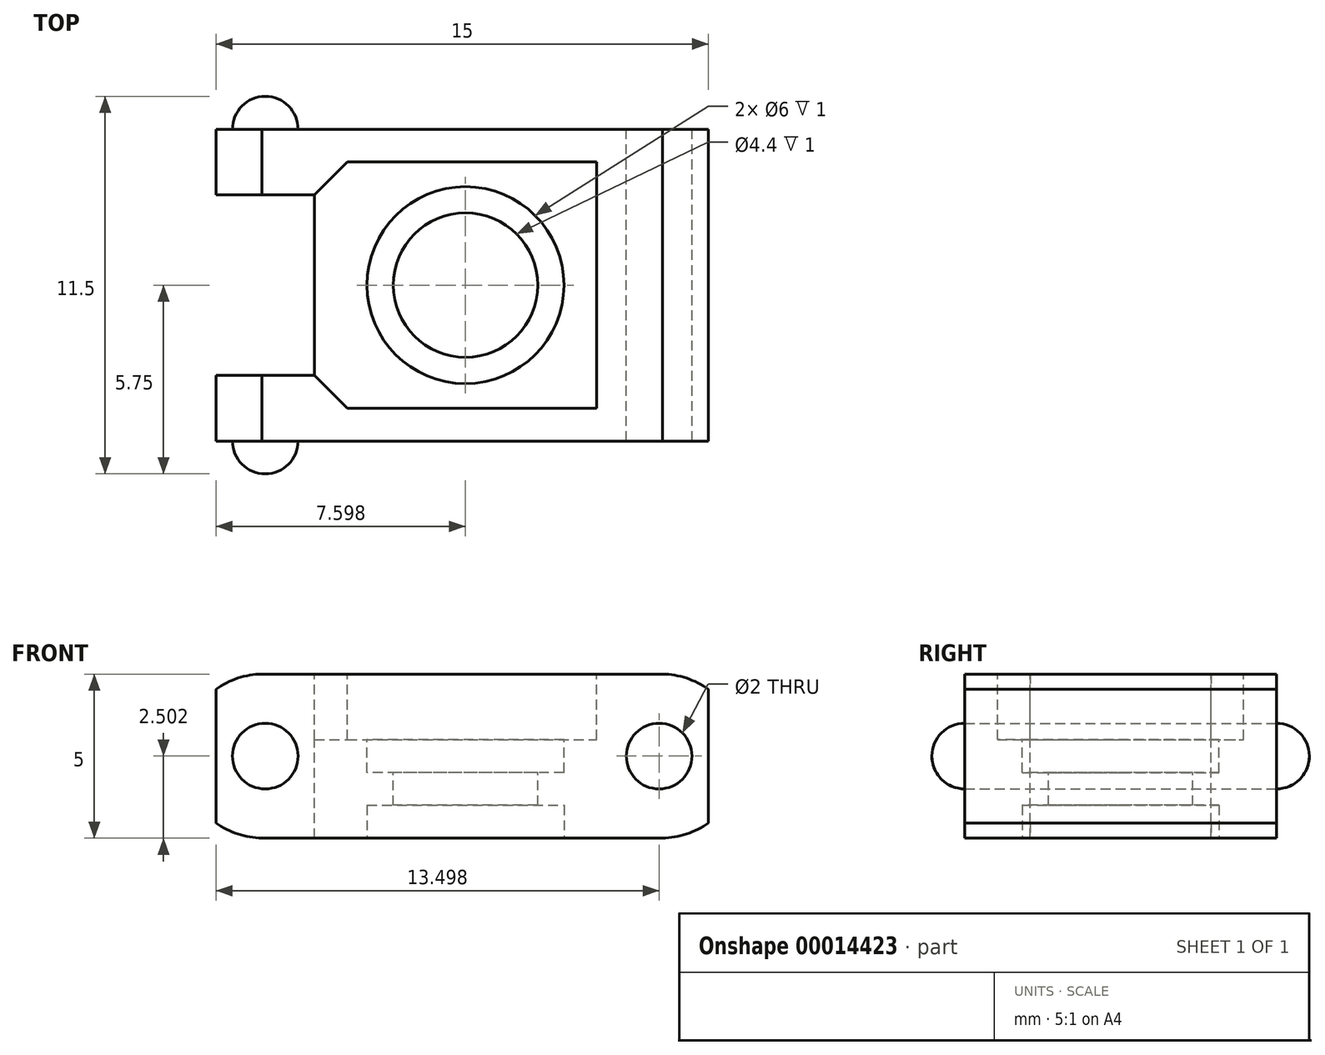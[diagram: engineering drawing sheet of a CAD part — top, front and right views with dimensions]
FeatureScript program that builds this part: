
annotation { "Feature Type Name" : "Feature", "Feature Type Description" : "" }
export const myFeature = defineFeature(function(context is Context, id is Id, definition is map)
    precondition{}
    {
        {
            var Q0;
            Q0=qCreatedBy(makeId("Front.planeOp"),FACE);
            var sketch = newSketch(context, id + "F0", { "sketchPlane" : qUnion([Q0])});
            skLineSegment(sketch, "E0.bottom", {"start": v(28.09, 13.2) * mm, "end": v(43.09, 13.2) * mm});
            skLineSegment(sketch, "E0.top", {"start": v(28.09, 8.2) * mm, "end": v(43.09, 8.2) * mm});
            skLineSegment(sketch, "E0.left", {"start": v(28.09, 13.2) * mm, "end": v(28.09, 8.2) * mm});
            skLineSegment(sketch, "E0.right", {"start": v(43.09, 13.2) * mm, "end": v(43.09, 8.2) * mm});
            skLineSegment(sketch, "E1", {"start": v(35.59, 8.2) * mm, "end": v(35.59, 13.2) * mm, "construction": true});
            skPoint(sketch, "E2", {"position": v(31.09, 13.2) * mm});
            skLineSegment(sketch, "E3", {"start": v(28.09, 8.2) * mm, "end": v(31.09, 13.2) * mm, "construction": true});
            skLineSegment(sketch, "E4", {"start": v(31.09, 13.2) * mm, "end": v(31.09, 8.2) * mm, "construction": true});
            skLineSegment(sketch, "E5", {"start": v(31.09, 8.2) * mm, "end": v(28.09, 13.2) * mm, "construction": true});
            skCircle(sketch, "E6", {"center": v(29.59, 10.7) * mm, "radius": 1 * mm});
            skLineSegment(sketch, "E7", {"start": v(29.59, 13.2) * mm, "end": v(29.59, 8.2) * mm, "construction": true});
            skLineSegment(sketch, "E8", {"start": v(28.09, 10.7) * mm, "end": v(31.09, 10.7) * mm, "construction": true});
            skArc(sketch, "E9", {"start": v(29.59, 13.2) * mm, "mid": v(27.04, 10.7) * mm, "end": v(29.59, 8.2) * mm});
            skCircle(sketch, "E10.0.MirrorC", {"center": v(41.59, 10.7) * mm, "radius": 1 * mm});
            skArc(sketch, "E11.0.MirrorCS", {"start": v(41.59, 13.2) * mm, "mid": v(44.14, 10.7) * mm, "end": v(41.59, 8.2) * mm});
            skSolve(sketch);
        }
        {
            var Q0;
            {var subQ5=sQuery(id+"F0.wireOp",EDGE,"E0.right");Q0=makeQuery(id+"F0.imprint","IMPRINT",FACE,{"disambiguationData":[TD([[makeQuery(id+"F0.imprint","IMPRINT",EDGE,{"derivedFrom":subQ5}),-1.0]])]});}
            var Q1;
            Q1=makeQuery(id+"F0.imprint","IMPRINT",FACE,{"disambiguationData":[TD([[makeQuery(id+"F0.imprint","IMPRINT",EDGE,{"derivedFrom":sQuery(id+"F0.wireOp",EDGE,"E6")}),-1.0]])]});
            var Q2;
            {var subQ5=sQuery(id+"F0.wireOp",EDGE,"E0.left");Q2=makeQuery(id+"F0.imprint","IMPRINT",FACE,{"disambiguationData":[TD([[makeQuery(id+"F0.imprint","IMPRINT",EDGE,{"derivedFrom":subQ5}),1.0]])]});}
            var Q3;
            Q3=makeQuery(id+"F0.imprint","IMPRINT",FACE,{"disambiguationData":[TD([[makeQuery(id+"F0.imprint","IMPRINT",EDGE,{"derivedFrom":sQuery(id+"F0.wireOp",EDGE,"E6")}),1.0]])]});
            var Q4;
            Q4=makeQuery(id+"F0.imprint","IMPRINT",FACE,{"disambiguationData":[TD([[makeQuery(id+"F0.imprint","IMPRINT",EDGE,{"derivedFrom":sQuery(id+"F0.wireOp",EDGE,"E10.0.MirrorC")}),-1.0]])]});
            extrude(context, id + "F1", {"entities" : qUnion([Q0, Q1, Q2, Q3, Q4]), "depth" : 9.5 * mm});
        }
        {
            var Q0;
            Q0=makeQuery(id+"F1.opExtrude","SWEPT_FACE",FACE,{"disambiguationData":[OSD([sQuery(id+"F0.wireOp",EDGE,"E0.bottom")])]});
            var sketch = newSketch(context, id + "F2", { "sketchPlane" : qUnion([Q0])});
            skLineSegment(sketch, "E12", {"start": v(35.59, 0) * mm, "end": v(35.59, -9.5) * mm, "construction": true});
            skLineSegment(sketch, "E13", {"start": v(28.09, -4.75) * mm, "end": v(43.09, -4.75) * mm, "construction": true});
            skPoint(sketch, "E14", {"position": v(31.09, 0) * mm});
            skLineSegment(sketch, "E15", {"start": v(31.09, 0) * mm, "end": v(31.09, -9.5) * mm, "construction": true});
            skPoint(sketch, "E16", {"position": v(28.09, -2) * mm});
            skLineSegment(sketch, "E17", {"start": v(28.09, -2) * mm, "end": v(31.09, -2) * mm});
            skLineSegment(sketch, "E18.0.MirrorCS", {"start": v(28.09, -7.5) * mm, "end": v(31.09, -7.5) * mm});
            skLineSegment(sketch, "E19", {"start": v(31.09, -7.5) * mm, "end": v(31.09, -2) * mm});
            skLineSegment(sketch, "E20", {"start": v(28.09, -2) * mm, "end": v(28.09, -7.5) * mm});
            skSolve(sketch);
        }
        {
            var Q0;
            Q0=makeQuery(id+"F2.imprint","IMPRINT",FACE,{"disambiguationData":[TD([[makeQuery(id+"F2.imprint","IMPRINT",EDGE,{"derivedFrom":sQuery(id+"F2.wireOp",EDGE,"E17")}),-1.0]])]});
            var Q1;
            Q1=makeQuery(id+"F2.imprint","IMPRINT",FACE,{"disambiguationData":[TD([[makeQuery(id+"F2.imprint","IMPRINT",EDGE,{"derivedFrom":sQuery(id+"F2.wireOp",EDGE,"8c34fa15-d911-4d8d-b620-4605c3a337e2.0.MirrorCS")}),-1.0]])]});
            extrude(context, id + "F3", {"entities" : qUnion([Q0, Q1]), "operationType" : NewBodyOperationType.REMOVE, "endBound" : BoundingType.THROUGH_ALL, "oppositeDirection" : true, "depth" : 25 * mm});
        }
        {
            var Q0;
            {var subQ5=sQuery(id+"F0.wireOp",EDGE,"E0.right");Q0=makeQuery(id+"F0.imprint","IMPRINT",FACE,{"disambiguationData":[TD([[makeQuery(id+"F0.imprint","IMPRINT",EDGE,{"derivedFrom":subQ5}),-1.0]])]});}
            var Q1;
            {var subQ5=sQuery(id+"F0.wireOp",EDGE,"E0.left");Q1=makeQuery(id+"F0.imprint","IMPRINT",FACE,{"disambiguationData":[TD([[makeQuery(id+"F0.imprint","IMPRINT",EDGE,{"derivedFrom":subQ5}),1.0]])]});}
            extrude(context, id + "F4", {"entities" : qUnion([Q0, Q1]), "operationType" : NewBodyOperationType.REMOVE, "endBound" : BoundingType.THROUGH_ALL, "depth" : 25 * mm});
        }
        {
            var Q0;
            Q0=makeQuery(id+"F0.imprint","IMPRINT",FACE,{"disambiguationData":[TD([[makeQuery(id+"F0.imprint","IMPRINT",EDGE,{"derivedFrom":sQuery(id+"F0.wireOp",EDGE,"E6")}),1.0]])]});
            extrude(context, id + "F5", {"entities" : qUnion([Q0]), "operationType" : NewBodyOperationType.ADD, "oppositeDirection" : true, "depth" : 1 * mm});
        }
        {
            var Q0;
            Q0=makeQuery(id+"F1.opExtrude","CAP_FACE",FACE,{"disambiguationData":[OSD([sQuery(id+"F0.wireOp",EDGE,"E0.bottom"),sQuery(id+"F0.wireOp",EDGE,"E0.top"),sQuery(id+"F0.wireOp",EDGE,"E0.left"),sQuery(id+"F0.wireOp",EDGE,"E0.right")])],"isStart":false});
            var sketch = newSketch(context, id + "F6", { "sketchPlane" : qUnion([Q0])});
            skLineSegment(sketch, "E21", {"start": v(35.59, 8.2) * mm, "end": v(35.59, 13.2) * mm, "construction": true});
            skPoint(sketch, "E22", {"position": v(31.09, 8.2) * mm});
            skPoint(sketch, "E23", {"position": v(28.09, 8.2) * mm});
            skLineSegment(sketch, "E24", {"start": v(31.09, 8.2) * mm, "end": v(31.09, 13.2) * mm, "construction": true});
            skLineSegment(sketch, "E25", {"start": v(31.09, 13.2) * mm, "end": v(28.09, 8.2) * mm, "construction": true});
            skPoint(sketch, "E26", {"position": v(28.09, 13.2) * mm});
            skLineSegment(sketch, "E27", {"start": v(28.09, 13.2) * mm, "end": v(28.09, 8.2) * mm, "construction": true});
            skLineSegment(sketch, "E28", {"start": v(31.09, 13.2) * mm, "end": v(28.09, 13.2) * mm, "construction": true});
            skLineSegment(sketch, "E29", {"start": v(28.09, 13.2) * mm, "end": v(31.09, 8.2) * mm, "construction": true});
            skCircle(sketch, "E30", {"center": v(29.59, 10.7) * mm, "radius": 1 * mm});
            skCircle(sketch, "E31.MirrorC", {"center": v(41.59, 10.7) * mm, "radius": 1 * mm});
            skSolve(sketch);
        }
        {
            var Q0;
            Q0=makeQuery(id+"F6.imprint","IMPRINT",FACE,{"disambiguationData":[TD([[makeQuery(id+"F6.imprint","IMPRINT",EDGE,{"derivedFrom":sQuery(id+"F6.wireOp",EDGE,"E30")}),1.0]])]});
            extrude(context, id + "F7", {"entities" : qUnion([Q0]), "operationType" : NewBodyOperationType.ADD, "depth" : 1 * mm, "hasSecondDirectionDraft" : true, "secondDirectionDraftAngle" : 10 * degree});
        }
        {
            var Q0;
            Q0=makeQuery(id+"F1.opExtrude","SWEPT_FACE",FACE,{"disambiguationData":[OSD([sQuery(id+"F0.wireOp",EDGE,"E0.bottom")])]});
            var sketch = newSketch(context, id + "F8", { "sketchPlane" : qUnion([Q0])});
            skPoint(sketch, "E32", {"position": v(31.09, -2) * mm});
            skPoint(sketch, "E33", {"position": v(31.09, -4.75) * mm});
            skLineSegment(sketch, "E34", {"start": v(31.09, -4.75) * mm, "end": v(41.69, -4.75) * mm, "construction": true});
            skPoint(sketch, "E35", {"position": v(39.69, -4.75) * mm});
            skLineSegment(sketch, "E36", {"start": v(31.09, -2) * mm, "end": v(41.69, -2) * mm, "construction": true});
            skLineSegment(sketch, "E37", {"start": v(39.69, -4.75) * mm, "end": v(39.69, -2) * mm});
            skLineSegment(sketch, "E38", {"start": v(31.09, -4.75) * mm, "end": v(31.09, -2) * mm});
            skLineSegment(sketch, "E39.MirrorCS", {"start": v(31.09, -4.75) * mm, "end": v(31.09, -7.5) * mm});
            skLineSegment(sketch, "E40.MirrorCS", {"start": v(39.69, -4.75) * mm, "end": v(39.69, -7.5) * mm});
            skPoint(sketch, "E41", {"position": v(41.69, -1) * mm});
            skPoint(sketch, "E42", {"position": v(41.69, 0) * mm});
            skLineSegment(sketch, "E43", {"start": v(41.69, -1) * mm, "end": v(31.09, -1) * mm, "construction": true});
            skPoint(sketch, "E44", {"position": v(32.09, -1) * mm});
            skLineSegment(sketch, "E45", {"start": v(31.09, -2) * mm, "end": v(31.09, -1) * mm, "construction": true});
            skLineSegment(sketch, "E46", {"start": v(31.09, -2) * mm, "end": v(32.09, -1) * mm});
            skPoint(sketch, "E47", {"position": v(39.69, -1) * mm});
            skLineSegment(sketch, "E48", {"start": v(32.09, -1) * mm, "end": v(39.69, -1) * mm});
            skLineSegment(sketch, "E49", {"start": v(39.69, -1) * mm, "end": v(39.69, -2) * mm});
            skLineSegment(sketch, "E50.MirrorCS", {"start": v(31.09, -7.5) * mm, "end": v(32.09, -8.5) * mm});
            skLineSegment(sketch, "E51.MirrorCS", {"start": v(32.09, -8.5) * mm, "end": v(39.69, -8.5) * mm});
            skLineSegment(sketch, "E52.MirrorCS", {"start": v(39.69, -8.5) * mm, "end": v(39.69, -7.5) * mm});
            skPoint(sketch, "E53.MirrorCS.end.orphan", {"position": v(31.09, -7.5) * mm});
            skPoint(sketch, "E53.MirrorCS.start.orphan", {"position": v(39.69, -7.5) * mm});
            skSolve(sketch);
        }
        {
            var Q0;
            Q0=makeQuery(id+"F8.imprint","IMPRINT",FACE,{"disambiguationData":[TD([[makeQuery(id+"F8.imprint","IMPRINT",EDGE,{"derivedFrom":sQuery(id+"F8.wireOp",EDGE,"E37")}),1.0]])]});
            extrude(context, id + "F9", {"entities" : qUnion([Q0]), "operationType" : NewBodyOperationType.REMOVE, "oppositeDirection" : true, "depth" : 2 * mm});
        }
        {
            var Q0;
            Q0=makeQuery(id+"F9.boolean.opBoolean","COPY",FACE,{"derivedFrom":makeQuery(id+"F9.opExtrude","CAP_FACE",FACE,{"disambiguationData":[OSD([sQuery(id+"F8.wireOp",EDGE,"E37"),sQuery(id+"F8.wireOp",EDGE,"1d8b683b-c03d-4aed-a5cb-2ff89669d674"),sQuery(id+"F8.wireOp",EDGE,"E38"),sQuery(id+"F8.wireOp",EDGE,"E53.MirrorCS"),sQuery(id+"F8.wireOp",EDGE,"E39.MirrorCS"),sQuery(id+"F8.wireOp",EDGE,"E40.MirrorCS")])],"isStart":false})});
            var sketch = newSketch(context, id + "F10", { "sketchPlane" : qUnion([Q0])});
            skPoint(sketch, "E54", {"position": v(31.09, -4.75) * mm});
            skPoint(sketch, "E55", {"position": v(39.69, -4.75) * mm});
            skLineSegment(sketch, "E56", {"start": v(31.09, -4.75) * mm, "end": v(39.69, -4.75) * mm, "construction": true});
            skPoint(sketch, "E57", {"position": v(35.69, -4.75) * mm});
            skPoint(sketch, "E58", {"position": v(32.83, -4.75) * mm});
            skCircle(sketch, "E59", {"center": v(35.69, -4.75) * mm, "radius": 3 * mm});
            skCircle(sketch, "E60", {"center": v(35.69, -4.75) * mm, "radius": 2.2 * mm});
            skSolve(sketch);
        }
        {
            var Q0;
            Q0=makeQuery(id+"F10.imprint","IMPRINT",FACE,{"disambiguationData":[TD([[makeQuery(id+"F10.imprint","IMPRINT",EDGE,{"derivedFrom":sQuery(id+"F10.wireOp",EDGE,"E60")}),1.0]])]});
            extrude(context, id + "F11", {"entities" : qUnion([Q0]), "operationType" : NewBodyOperationType.REMOVE, "endBound" : BoundingType.THROUGH_ALL, "oppositeDirection" : true, "depth" : 25 * mm});
        }
        {
            var Q0;
            Q0=makeQuery(id+"F10.imprint","IMPRINT",FACE,{"disambiguationData":[TD([[makeQuery(id+"F10.imprint","IMPRINT",EDGE,{"derivedFrom":sQuery(id+"F10.wireOp",EDGE,"E59")}),1.0]])]});
            extrude(context, id + "F12", {"entities" : qUnion([Q0]), "operationType" : NewBodyOperationType.REMOVE, "oppositeDirection" : true, "depth" : 1 * mm});
        }
        {
            var Q0;
            Q0=makeQuery(id+"F1.opExtrude","SWEPT_FACE",FACE,{"disambiguationData":[OSD([sQuery(id+"F0.wireOp",EDGE,"E0.top")])]});
            var sketch = newSketch(context, id + "F13", { "sketchPlane" : qUnion([Q0])});
            skCircle(sketch, "E61", {"center": v(35.69, 4.75) * mm, "radius": 3 * mm});
            skCircle(sketch, "E62", {"center": v(35.69, 4.75) * mm, "radius": 2.2 * mm});
            skSolve(sketch);
        }
        {
            var Q0;
            Q0=makeQuery(id+"F13.imprint","IMPRINT",FACE,{"disambiguationData":[TD([[makeQuery(id+"F13.imprint","IMPRINT",EDGE,{"derivedFrom":sQuery(id+"F13.wireOp",EDGE,"E61")}),1.0]])]});
            extrude(context, id + "F14", {"entities" : qUnion([Q0]), "operationType" : NewBodyOperationType.REMOVE, "oppositeDirection" : true, "depth" : 1 * mm});
        }
        {
            var Q0;
            Q0=makeQuery(id+"F5.opExtrude","CAP_EDGE",EDGE,{"disambiguationData":[OSD([sQuery(id+"F0.wireOp",EDGE,"E6")])],"isStart":false});
            var Q1;
            Q1=makeQuery(id+"F7.opExtrude","CAP_EDGE",EDGE,{"disambiguationData":[OSD([sQuery(id+"F6.wireOp",EDGE,"E30")])],"isStart":false});
            fillet(context, id + "F15", {"entities" : qUnion([Q0, Q1]), "radius" : 1 * mm, "tangentPropagation" : true, "allowEdgeOverflow" : false});
        }
    });
